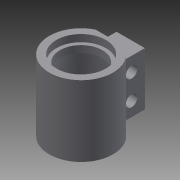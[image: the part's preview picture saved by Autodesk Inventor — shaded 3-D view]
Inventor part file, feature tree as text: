
AUTODESK INVENTOR PART (.ipt)
format: ipt  version: 2013 SP2 (Build 170200200, 200)  size: 140,800 bytes
history: native  units: mm
features: extrude x3, revolve x1, sketch x1
ambient origin geometry x8: Origin, YZ Plane, XZ Plane, XY Plane, X Axis, Y Axis, Z Axis, Center Point
bodies: Solid1 (feature_tree)
feature tree (5):
  revolve  "Revolution1"  Angle=90.0deg
  extrude  "Extrusion1"  Depth=2.0mm
  extrude  "Extrusion2"  TaperAngle=0.0deg  [1 undecoded]
  extrude  "Extrusion3"  Depth=2.0mm
  sketch  "Sketch4"  dims[d2=18.0mm d7=90.0deg d12=2.0mm d14=0.0mm d16=2.0mm d17=7.0mm d20=8.0mm d21=0.0mm d28=14.0mm d29=3.2mm d30=3.2mm d31=7.0mm d32=10.0mm d33=0.0mm d34=3.75mm d35=16.580628mm d36=9.0mm d47=15.0mm d49=4.0mm d50=4.0mm d51=10.0mm d52=0.0mm d57=2.0mm d60=6.0mm]
note: 1 required parameter value undecoded (feature->parameter linkage not recoverable at this tier; creation-order binding heuristic only, values carry confidence <= 0.55)
